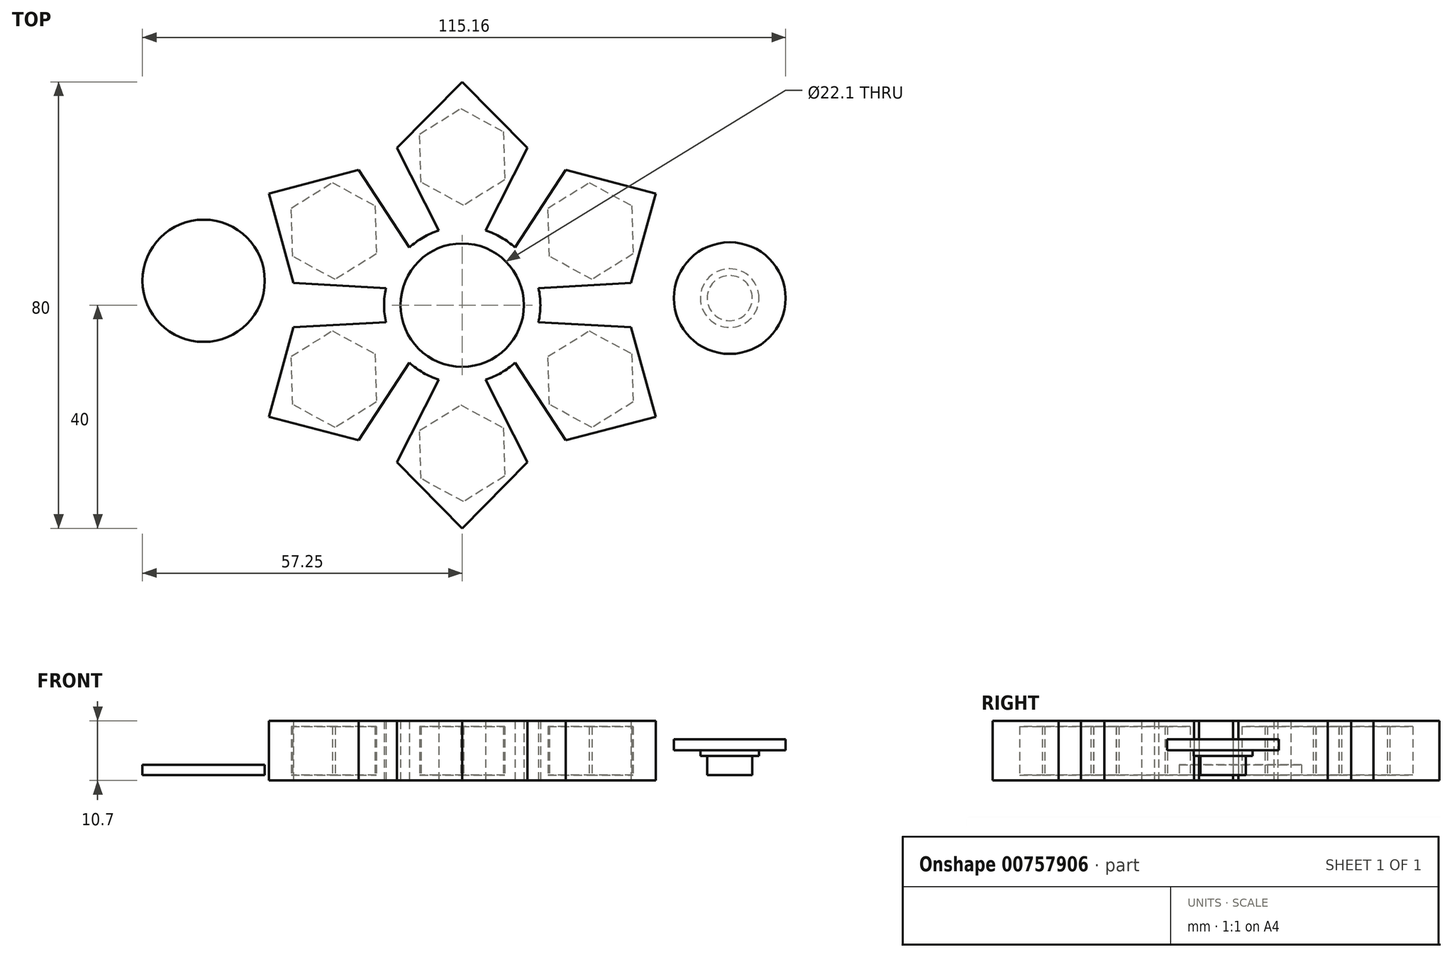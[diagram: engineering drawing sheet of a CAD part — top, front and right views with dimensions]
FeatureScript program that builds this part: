
annotation { "Feature Type Name" : "Feature", "Feature Type Description" : "" }
export const myFeature = defineFeature(function(context is Context, id is Id, definition is map)
    precondition{}
    {
        {
            var Q0;
            Q0=qCreatedBy(makeId("Top.planeOp"),FACE);
            var sketch = newSketch(context, id + "F0", { "sketchPlane" : qUnion([Q0])});
            skCircle(sketch, "E0.cCircle", {"center": v(0, 26.55) * mm, "radius": 8.66 * mm, "construction": true});
            skLineSegment(sketch, "E0.0", {"start": v(7.63, 22.44) * mm, "end": v(0.26, 17.9) * mm});
            skLineSegment(sketch, "E0.1", {"start": v(0.26, 17.9) * mm, "end": v(-7.37, 22) * mm});
            skLineSegment(sketch, "E0.2", {"start": v(-7.37, 22) * mm, "end": v(-7.63, 30.66) * mm});
            skLineSegment(sketch, "E0.3", {"start": v(-7.63, 30.66) * mm, "end": v(-0.26, 35.2) * mm});
            skLineSegment(sketch, "E0.4", {"start": v(-0.26, 35.2) * mm, "end": v(7.37, 31.1) * mm});
            skLineSegment(sketch, "E0.5", {"start": v(7.37, 31.1) * mm, "end": v(7.63, 22.44) * mm});
            skCircle(sketch, "E1", {"center": v(0, 0) * mm, "radius": 40 * mm, "construction": true});
            skCircle(sketch, "E2", {"center": v(0, 0) * mm, "radius": 11.05 * mm});
            skLineSegment(sketch, "E3", {"start": v(0, 40) * mm, "end": v(-11.68, 28.18) * mm});
            skCircle(sketch, "E4", {"center": v(0, 0) * mm, "radius": 14 * mm});
            skLineSegment(sketch, "E5", {"start": v(-11.68, 28.18) * mm, "end": v(-4.19, 13.36) * mm});
            skLineSegment(sketch, "E6", {"start": v(0, 0) * mm, "end": v(0, 60.04) * mm, "construction": true});
            skLineSegment(sketch, "E7.MirrorCS", {"start": v(11.68, 28.18) * mm, "end": v(4.19, 13.36) * mm});
            skLineSegment(sketch, "E8.MirrorCS", {"start": v(0, 40) * mm, "end": v(11.68, 28.18) * mm});
            skLineSegment(sketch, "E9.1.0", {"start": v(-34.64, 20) * mm, "end": v(-30.25, 3.97) * mm});
            skLineSegment(sketch, "E9.1.1", {"start": v(-23.25, 21.93) * mm, "end": v(-15.62, 17.83) * mm});
            skLineSegment(sketch, "E9.1.2", {"start": v(-30.62, 17.38) * mm, "end": v(-23.25, 21.93) * mm});
            skLineSegment(sketch, "E9.1.3", {"start": v(-30.36, 8.72) * mm, "end": v(-30.62, 17.38) * mm});
            skLineSegment(sketch, "E9.1.4", {"start": v(-22.74, 4.62) * mm, "end": v(-30.36, 8.72) * mm});
            skLineSegment(sketch, "E9.1.5", {"start": v(-15.37, 9.17) * mm, "end": v(-22.74, 4.62) * mm});
            skLineSegment(sketch, "E9.1.6", {"start": v(-15.62, 17.83) * mm, "end": v(-15.37, 9.17) * mm});
            skLineSegment(sketch, "E9.1.7", {"start": v(-30.25, 3.97) * mm, "end": v(-13.66, 3.05) * mm});
            skCircle(sketch, "E9.1.8", {"center": v(-23, 13.27) * mm, "radius": 8.66 * mm, "construction": true});
            skLineSegment(sketch, "E9.1.9", {"start": v(-18.57, 24.2) * mm, "end": v(-9.47, 10.3) * mm});
            skLineSegment(sketch, "E9.1.10", {"start": v(-34.64, 20) * mm, "end": v(-18.57, 24.2) * mm});
            skLineSegment(sketch, "E9.2.0", {"start": v(-34.64, -20) * mm, "end": v(-18.57, -24.2) * mm});
            skLineSegment(sketch, "E9.2.1", {"start": v(-30.62, -9.17) * mm, "end": v(-23.25, -4.62) * mm});
            skLineSegment(sketch, "E9.2.2", {"start": v(-30.36, -17.83) * mm, "end": v(-30.62, -9.17) * mm});
            skLineSegment(sketch, "E9.2.3", {"start": v(-22.74, -21.93) * mm, "end": v(-30.36, -17.83) * mm});
            skLineSegment(sketch, "E9.2.4", {"start": v(-15.37, -17.38) * mm, "end": v(-22.74, -21.93) * mm});
            skLineSegment(sketch, "E9.2.5", {"start": v(-15.62, -8.72) * mm, "end": v(-15.37, -17.38) * mm});
            skLineSegment(sketch, "E9.2.6", {"start": v(-23.25, -4.62) * mm, "end": v(-15.62, -8.72) * mm});
            skLineSegment(sketch, "E9.2.7", {"start": v(-18.57, -24.2) * mm, "end": v(-9.47, -10.3) * mm});
            skCircle(sketch, "E9.2.8", {"center": v(-23, -13.27) * mm, "radius": 8.66 * mm, "construction": true});
            skLineSegment(sketch, "E9.2.9", {"start": v(-30.25, -3.97) * mm, "end": v(-13.66, -3.05) * mm});
            skLineSegment(sketch, "E9.2.10", {"start": v(-34.64, -20) * mm, "end": v(-30.25, -3.97) * mm});
            skLineSegment(sketch, "E9.3.0", {"start": v(0, -40) * mm, "end": v(11.68, -28.18) * mm});
            skLineSegment(sketch, "E9.3.1", {"start": v(-7.37, -31.1) * mm, "end": v(-7.63, -22.44) * mm});
            skLineSegment(sketch, "E9.3.2", {"start": v(0.26, -35.2) * mm, "end": v(-7.37, -31.1) * mm});
            skLineSegment(sketch, "E9.3.3", {"start": v(7.63, -30.66) * mm, "end": v(0.26, -35.2) * mm});
            skLineSegment(sketch, "E9.3.4", {"start": v(7.37, -22) * mm, "end": v(7.63, -30.66) * mm});
            skLineSegment(sketch, "E9.3.5", {"start": v(-0.26, -17.9) * mm, "end": v(7.37, -22) * mm});
            skLineSegment(sketch, "E9.3.6", {"start": v(-7.63, -22.44) * mm, "end": v(-0.26, -17.9) * mm});
            skLineSegment(sketch, "E9.3.7", {"start": v(11.68, -28.18) * mm, "end": v(4.19, -13.36) * mm});
            skCircle(sketch, "E9.3.8", {"center": v(0, -26.55) * mm, "radius": 8.66 * mm, "construction": true});
            skLineSegment(sketch, "E9.3.9", {"start": v(-11.68, -28.18) * mm, "end": v(-4.19, -13.36) * mm});
            skLineSegment(sketch, "E9.3.10", {"start": v(0, -40) * mm, "end": v(-11.68, -28.18) * mm});
            skLineSegment(sketch, "E9.4.0", {"start": v(34.64, -20) * mm, "end": v(30.25, -3.97) * mm});
            skLineSegment(sketch, "E9.4.1", {"start": v(23.25, -21.93) * mm, "end": v(15.62, -17.83) * mm});
            skLineSegment(sketch, "E9.4.2", {"start": v(30.62, -17.38) * mm, "end": v(23.25, -21.93) * mm});
            skLineSegment(sketch, "E9.4.3", {"start": v(30.36, -8.72) * mm, "end": v(30.62, -17.38) * mm});
            skLineSegment(sketch, "E9.4.4", {"start": v(22.74, -4.62) * mm, "end": v(30.36, -8.72) * mm});
            skLineSegment(sketch, "E9.4.5", {"start": v(15.37, -9.17) * mm, "end": v(22.74, -4.62) * mm});
            skLineSegment(sketch, "E9.4.6", {"start": v(15.62, -17.83) * mm, "end": v(15.37, -9.17) * mm});
            skLineSegment(sketch, "E9.4.7", {"start": v(30.25, -3.97) * mm, "end": v(13.66, -3.05) * mm});
            skCircle(sketch, "E9.4.8", {"center": v(23, -13.27) * mm, "radius": 8.66 * mm, "construction": true});
            skLineSegment(sketch, "E9.4.9", {"start": v(18.57, -24.2) * mm, "end": v(9.47, -10.3) * mm});
            skLineSegment(sketch, "E9.4.10", {"start": v(34.64, -20) * mm, "end": v(18.57, -24.2) * mm});
            skLineSegment(sketch, "E9.5.0", {"start": v(34.64, 20) * mm, "end": v(18.57, 24.2) * mm});
            skLineSegment(sketch, "E9.5.1", {"start": v(30.62, 9.17) * mm, "end": v(23.25, 4.62) * mm});
            skLineSegment(sketch, "E9.5.2", {"start": v(30.36, 17.83) * mm, "end": v(30.62, 9.17) * mm});
            skLineSegment(sketch, "E9.5.3", {"start": v(22.74, 21.93) * mm, "end": v(30.36, 17.83) * mm});
            skLineSegment(sketch, "E9.5.4", {"start": v(15.37, 17.38) * mm, "end": v(22.74, 21.93) * mm});
            skLineSegment(sketch, "E9.5.5", {"start": v(15.62, 8.72) * mm, "end": v(15.37, 17.38) * mm});
            skLineSegment(sketch, "E9.5.6", {"start": v(23.25, 4.62) * mm, "end": v(15.62, 8.72) * mm});
            skLineSegment(sketch, "E9.5.7", {"start": v(18.57, 24.2) * mm, "end": v(9.47, 10.3) * mm});
            skCircle(sketch, "E9.5.8", {"center": v(23, 13.27) * mm, "radius": 8.66 * mm, "construction": true});
            skLineSegment(sketch, "E9.5.9", {"start": v(30.25, 3.97) * mm, "end": v(13.66, 3.05) * mm});
            skLineSegment(sketch, "E9.5.10", {"start": v(34.64, 20) * mm, "end": v(30.25, 3.97) * mm});
            skSolve(sketch);
        }
        {
            var Q0;
            Q0=makeQuery(id+"F0.imprint","IMPRINT",FACE,{"disambiguationData":[TD([[makeQuery(id+"F0.imprint","IMPRINT",EDGE,{"derivedFrom":sQuery(id+"F0.wireOp",EDGE,"E9.1.0")}),1.0]])]});
            var Q1;
            Q1=makeQuery(id+"F0.imprint","IMPRINT",FACE,{"disambiguationData":[TD([[makeQuery(id+"F0.imprint","IMPRINT",EDGE,{"derivedFrom":sQuery(id+"F0.wireOp",EDGE,"E0.0")}),1.0]])]});
            var Q2;
            Q2=makeQuery(id+"F0.imprint","IMPRINT",FACE,{"disambiguationData":[TD([[makeQuery(id+"F0.imprint","IMPRINT",EDGE,{"derivedFrom":sQuery(id+"F0.wireOp",EDGE,"E9.5.0")}),1.0]])]});
            var Q3;
            Q3=makeQuery(id+"F0.imprint","IMPRINT",FACE,{"disambiguationData":[TD([[makeQuery(id+"F0.imprint","IMPRINT",EDGE,{"derivedFrom":sQuery(id+"F0.wireOp",EDGE,"E9.4.0")}),1.0]])]});
            var Q4;
            Q4=makeQuery(id+"F0.imprint","IMPRINT",FACE,{"disambiguationData":[TD([[makeQuery(id+"F0.imprint","IMPRINT",EDGE,{"derivedFrom":sQuery(id+"F0.wireOp",EDGE,"E9.3.0")}),1.0]])]});
            var Q5;
            Q5=makeQuery(id+"F0.imprint","IMPRINT",FACE,{"disambiguationData":[TD([[makeQuery(id+"F0.imprint","IMPRINT",EDGE,{"derivedFrom":sQuery(id+"F0.wireOp",EDGE,"E9.2.0")}),1.0]])]});
            var Q6;
            Q6=makeQuery(id+"F0.imprint","IMPRINT",FACE,{"disambiguationData":[TD([[makeQuery(id+"F0.imprint","IMPRINT",EDGE,{"derivedFrom":sQuery(id+"F0.wireOp",EDGE,"E2")}),-1.0]])]});
            extrude(context, id + "F1", {"entities" : qUnion([Q0, Q1, Q2, Q3, Q4, Q5, Q6]), "depth" : 8.7 * mm, "offsetDistance" : 25 * mm});
        }
        {
            var Q0;
            Q0=makeQuery(id+"F1.opExtrude","CAP_FACE",FACE,{"disambiguationData":[OSD([sQuery(id+"F0.wireOp",EDGE,"E0.0"),sQuery(id+"F0.wireOp",EDGE,"E0.1"),sQuery(id+"F0.wireOp",EDGE,"E0.2"),sQuery(id+"F0.wireOp",EDGE,"E0.3"),sQuery(id+"F0.wireOp",EDGE,"E0.4"),sQuery(id+"F0.wireOp",EDGE,"E0.5"),sQuery(id+"F0.wireOp",EDGE,"E2"),sQuery(id+"F0.wireOp",EDGE,"E3"),sQuery(id+"F0.wireOp",EDGE,"E4"),sQuery(id+"F0.wireOp",EDGE,"E5"),sQuery(id+"F0.wireOp",EDGE,"E7.MirrorCS"),sQuery(id+"F0.wireOp",EDGE,"E8.MirrorCS"),sQuery(id+"F0.wireOp",EDGE,"E9.1.0"),sQuery(id+"F0.wireOp",EDGE,"E9.1.1"),sQuery(id+"F0.wireOp",EDGE,"E9.1.2"),sQuery(id+"F0.wireOp",EDGE,"E9.1.3"),sQuery(id+"F0.wireOp",EDGE,"E9.1.4"),sQuery(id+"F0.wireOp",EDGE,"E9.1.5"),sQuery(id+"F0.wireOp",EDGE,"E9.1.6"),sQuery(id+"F0.wireOp",EDGE,"E9.1.7"),sQuery(id+"F0.wireOp",EDGE,"E9.1.9"),sQuery(id+"F0.wireOp",EDGE,"E9.1.10"),sQuery(id+"F0.wireOp",EDGE,"E9.2.0"),sQuery(id+"F0.wireOp",EDGE,"E9.2.1"),sQuery(id+"F0.wireOp",EDGE,"E9.2.2"),sQuery(id+"F0.wireOp",EDGE,"E9.2.3"),sQuery(id+"F0.wireOp",EDGE,"E9.2.4"),sQuery(id+"F0.wireOp",EDGE,"E9.2.5"),sQuery(id+"F0.wireOp",EDGE,"E9.2.6"),sQuery(id+"F0.wireOp",EDGE,"E9.2.7"),sQuery(id+"F0.wireOp",EDGE,"E9.2.9"),sQuery(id+"F0.wireOp",EDGE,"E9.2.10"),sQuery(id+"F0.wireOp",EDGE,"E9.3.0"),sQuery(id+"F0.wireOp",EDGE,"E9.3.1"),sQuery(id+"F0.wireOp",EDGE,"E9.3.2"),sQuery(id+"F0.wireOp",EDGE,"E9.3.3"),sQuery(id+"F0.wireOp",EDGE,"E9.3.4"),sQuery(id+"F0.wireOp",EDGE,"E9.3.5"),sQuery(id+"F0.wireOp",EDGE,"E9.3.6"),sQuery(id+"F0.wireOp",EDGE,"E9.3.7"),sQuery(id+"F0.wireOp",EDGE,"E9.3.9"),sQuery(id+"F0.wireOp",EDGE,"E9.3.10"),sQuery(id+"F0.wireOp",EDGE,"E9.4.0"),sQuery(id+"F0.wireOp",EDGE,"E9.4.1"),sQuery(id+"F0.wireOp",EDGE,"E9.4.2"),sQuery(id+"F0.wireOp",EDGE,"E9.4.3"),sQuery(id+"F0.wireOp",EDGE,"E9.4.4"),sQuery(id+"F0.wireOp",EDGE,"E9.4.5"),sQuery(id+"F0.wireOp",EDGE,"E9.4.6"),sQuery(id+"F0.wireOp",EDGE,"E9.4.7"),sQuery(id+"F0.wireOp",EDGE,"E9.4.9"),sQuery(id+"F0.wireOp",EDGE,"E9.4.10"),sQuery(id+"F0.wireOp",EDGE,"E9.5.0"),sQuery(id+"F0.wireOp",EDGE,"E9.5.1"),sQuery(id+"F0.wireOp",EDGE,"E9.5.2"),sQuery(id+"F0.wireOp",EDGE,"E9.5.3"),sQuery(id+"F0.wireOp",EDGE,"E9.5.4"),sQuery(id+"F0.wireOp",EDGE,"E9.5.5"),sQuery(id+"F0.wireOp",EDGE,"E9.5.6"),sQuery(id+"F0.wireOp",EDGE,"E9.5.7"),sQuery(id+"F0.wireOp",EDGE,"E9.5.9"),sQuery(id+"F0.wireOp",EDGE,"E9.5.10")])],"isStart":false});
            var sketch = newSketch(context, id + "F2", { "sketchPlane" : qUnion([Q0])});
            skLineSegment(sketch, "E10.0", {"start": v(-34.64, 20) * mm, "end": v(-30.25, 3.97) * mm});
            skLineSegment(sketch, "E10.1", {"start": v(-34.64, 20) * mm, "end": v(-18.57, 24.2) * mm});
            skLineSegment(sketch, "E10.2", {"start": v(-18.57, 24.2) * mm, "end": v(-9.47, 10.3) * mm});
            skCircle(sketch, "E10.3", {"center": v(0, 0) * mm, "radius": 14 * mm});
            skLineSegment(sketch, "E10.4", {"start": v(-11.68, 28.18) * mm, "end": v(-4.19, 13.36) * mm});
            skLineSegment(sketch, "E10.5", {"start": v(0, 40) * mm, "end": v(-11.68, 28.18) * mm});
            skLineSegment(sketch, "E10.6", {"start": v(0, 40) * mm, "end": v(11.68, 28.18) * mm});
            skLineSegment(sketch, "E10.7", {"start": v(11.68, 28.18) * mm, "end": v(4.19, 13.36) * mm});
            skLineSegment(sketch, "E10.8", {"start": v(18.57, 24.2) * mm, "end": v(9.47, 10.3) * mm});
            skLineSegment(sketch, "E10.9", {"start": v(34.64, 20) * mm, "end": v(18.57, 24.2) * mm});
            skLineSegment(sketch, "E10.10", {"start": v(34.64, 20) * mm, "end": v(30.25, 3.97) * mm});
            skLineSegment(sketch, "E10.11", {"start": v(30.25, 3.97) * mm, "end": v(13.66, 3.05) * mm});
            skLineSegment(sketch, "E10.12", {"start": v(30.25, -3.97) * mm, "end": v(13.66, -3.05) * mm});
            skLineSegment(sketch, "E10.13", {"start": v(34.64, -20) * mm, "end": v(30.25, -3.97) * mm});
            skLineSegment(sketch, "E10.14", {"start": v(34.64, -20) * mm, "end": v(18.57, -24.2) * mm});
            skLineSegment(sketch, "E10.15", {"start": v(18.57, -24.2) * mm, "end": v(9.47, -10.3) * mm});
            skLineSegment(sketch, "E10.16", {"start": v(11.68, -28.18) * mm, "end": v(4.19, -13.36) * mm});
            skLineSegment(sketch, "E10.17", {"start": v(0, -40) * mm, "end": v(11.68, -28.18) * mm});
            skLineSegment(sketch, "E10.18", {"start": v(0, -40) * mm, "end": v(-11.68, -28.18) * mm});
            skLineSegment(sketch, "E10.19", {"start": v(-11.68, -28.18) * mm, "end": v(-4.19, -13.36) * mm});
            skLineSegment(sketch, "E10.20", {"start": v(-18.57, -24.2) * mm, "end": v(-9.47, -10.3) * mm});
            skLineSegment(sketch, "E10.21", {"start": v(-34.64, -20) * mm, "end": v(-18.57, -24.2) * mm});
            skLineSegment(sketch, "E10.22", {"start": v(-34.64, -20) * mm, "end": v(-30.25, -3.97) * mm});
            skLineSegment(sketch, "E10.23", {"start": v(-30.25, -3.97) * mm, "end": v(-13.66, -3.05) * mm});
            skLineSegment(sketch, "E10.24", {"start": v(-30.25, 3.97) * mm, "end": v(-13.66, 3.05) * mm});
            skCircle(sketch, "E10.25", {"center": v(0, 0) * mm, "radius": 11.05 * mm});
            skSolve(sketch);
        }
        {
            var Q0;
            Q0 = qSketchRegion(id + "F2", true);
            extrude(context, id + "F3", {"entities" : qUnion([Q0]), "operationType" : NewBodyOperationType.ADD, "depth" : 1 * mm, "offsetDistance" : 25 * mm});
        }
        {
            var Q0;
            Q0=makeQuery(id+"F1.opExtrude","CAP_FACE",FACE,{"disambiguationData":[OSD([sQuery(id+"F0.wireOp",EDGE,"E0.0"),sQuery(id+"F0.wireOp",EDGE,"E0.1"),sQuery(id+"F0.wireOp",EDGE,"E0.2"),sQuery(id+"F0.wireOp",EDGE,"E0.3"),sQuery(id+"F0.wireOp",EDGE,"E0.4"),sQuery(id+"F0.wireOp",EDGE,"E0.5"),sQuery(id+"F0.wireOp",EDGE,"E2"),sQuery(id+"F0.wireOp",EDGE,"E3"),sQuery(id+"F0.wireOp",EDGE,"E4"),sQuery(id+"F0.wireOp",EDGE,"E5"),sQuery(id+"F0.wireOp",EDGE,"E7.MirrorCS"),sQuery(id+"F0.wireOp",EDGE,"E8.MirrorCS"),sQuery(id+"F0.wireOp",EDGE,"E9.1.0"),sQuery(id+"F0.wireOp",EDGE,"E9.1.1"),sQuery(id+"F0.wireOp",EDGE,"E9.1.2"),sQuery(id+"F0.wireOp",EDGE,"E9.1.3"),sQuery(id+"F0.wireOp",EDGE,"E9.1.4"),sQuery(id+"F0.wireOp",EDGE,"E9.1.5"),sQuery(id+"F0.wireOp",EDGE,"E9.1.6"),sQuery(id+"F0.wireOp",EDGE,"E9.1.7"),sQuery(id+"F0.wireOp",EDGE,"E9.1.9"),sQuery(id+"F0.wireOp",EDGE,"E9.1.10"),sQuery(id+"F0.wireOp",EDGE,"E9.2.0"),sQuery(id+"F0.wireOp",EDGE,"E9.2.1"),sQuery(id+"F0.wireOp",EDGE,"E9.2.2"),sQuery(id+"F0.wireOp",EDGE,"E9.2.3"),sQuery(id+"F0.wireOp",EDGE,"E9.2.4"),sQuery(id+"F0.wireOp",EDGE,"E9.2.5"),sQuery(id+"F0.wireOp",EDGE,"E9.2.6"),sQuery(id+"F0.wireOp",EDGE,"E9.2.7"),sQuery(id+"F0.wireOp",EDGE,"E9.2.9"),sQuery(id+"F0.wireOp",EDGE,"E9.2.10"),sQuery(id+"F0.wireOp",EDGE,"E9.3.0"),sQuery(id+"F0.wireOp",EDGE,"E9.3.1"),sQuery(id+"F0.wireOp",EDGE,"E9.3.2"),sQuery(id+"F0.wireOp",EDGE,"E9.3.3"),sQuery(id+"F0.wireOp",EDGE,"E9.3.4"),sQuery(id+"F0.wireOp",EDGE,"E9.3.5"),sQuery(id+"F0.wireOp",EDGE,"E9.3.6"),sQuery(id+"F0.wireOp",EDGE,"E9.3.7"),sQuery(id+"F0.wireOp",EDGE,"E9.3.9"),sQuery(id+"F0.wireOp",EDGE,"E9.3.10"),sQuery(id+"F0.wireOp",EDGE,"E9.4.0"),sQuery(id+"F0.wireOp",EDGE,"E9.4.1"),sQuery(id+"F0.wireOp",EDGE,"E9.4.2"),sQuery(id+"F0.wireOp",EDGE,"E9.4.3"),sQuery(id+"F0.wireOp",EDGE,"E9.4.4"),sQuery(id+"F0.wireOp",EDGE,"E9.4.5"),sQuery(id+"F0.wireOp",EDGE,"E9.4.6"),sQuery(id+"F0.wireOp",EDGE,"E9.4.7"),sQuery(id+"F0.wireOp",EDGE,"E9.4.9"),sQuery(id+"F0.wireOp",EDGE,"E9.4.10"),sQuery(id+"F0.wireOp",EDGE,"E9.5.0"),sQuery(id+"F0.wireOp",EDGE,"E9.5.1"),sQuery(id+"F0.wireOp",EDGE,"E9.5.2"),sQuery(id+"F0.wireOp",EDGE,"E9.5.3"),sQuery(id+"F0.wireOp",EDGE,"E9.5.4"),sQuery(id+"F0.wireOp",EDGE,"E9.5.5"),sQuery(id+"F0.wireOp",EDGE,"E9.5.6"),sQuery(id+"F0.wireOp",EDGE,"E9.5.7"),sQuery(id+"F0.wireOp",EDGE,"E9.5.9"),sQuery(id+"F0.wireOp",EDGE,"E9.5.10")])],"isStart":true});
            var sketch = newSketch(context, id + "F4", { "sketchPlane" : qUnion([Q0])});
            skCircle(sketch, "E11.0", {"center": v(0, 0) * mm, "radius": 11.05 * mm});
            skCircle(sketch, "E11.1", {"center": v(0, 0) * mm, "radius": 14 * mm});
            skLineSegment(sketch, "E11.2", {"start": v(-11.68, 28.18) * mm, "end": v(-4.19, 13.36) * mm});
            skLineSegment(sketch, "E11.3", {"start": v(11.68, 28.18) * mm, "end": v(4.19, 13.36) * mm});
            skLineSegment(sketch, "E11.4", {"start": v(0, 40) * mm, "end": v(11.68, 28.18) * mm});
            skLineSegment(sketch, "E11.5", {"start": v(0, 40) * mm, "end": v(-11.68, 28.18) * mm});
            skLineSegment(sketch, "E12.1.0", {"start": v(-30.25, 3.97) * mm, "end": v(-13.66, 3.05) * mm});
            skLineSegment(sketch, "E12.1.1", {"start": v(-34.64, 20) * mm, "end": v(-30.25, 3.97) * mm});
            skLineSegment(sketch, "E12.1.2", {"start": v(-34.64, 20) * mm, "end": v(-18.57, 24.2) * mm});
            skLineSegment(sketch, "E12.1.3", {"start": v(-18.57, 24.2) * mm, "end": v(-9.47, 10.3) * mm});
            skLineSegment(sketch, "E12.2.0", {"start": v(-18.57, -24.2) * mm, "end": v(-9.47, -10.3) * mm});
            skLineSegment(sketch, "E12.2.1", {"start": v(-34.64, -20) * mm, "end": v(-18.57, -24.2) * mm});
            skLineSegment(sketch, "E12.2.2", {"start": v(-34.64, -20) * mm, "end": v(-30.25, -3.97) * mm});
            skLineSegment(sketch, "E12.2.3", {"start": v(-30.25, -3.97) * mm, "end": v(-13.66, -3.05) * mm});
            skLineSegment(sketch, "E12.3.0", {"start": v(11.68, -28.18) * mm, "end": v(4.19, -13.36) * mm});
            skLineSegment(sketch, "E12.3.1", {"start": v(0, -40) * mm, "end": v(11.68, -28.18) * mm});
            skLineSegment(sketch, "E12.3.2", {"start": v(0, -40) * mm, "end": v(-11.68, -28.18) * mm});
            skLineSegment(sketch, "E12.3.3", {"start": v(-11.68, -28.18) * mm, "end": v(-4.19, -13.36) * mm});
            skLineSegment(sketch, "E12.4.0", {"start": v(30.25, -3.97) * mm, "end": v(13.66, -3.05) * mm});
            skLineSegment(sketch, "E12.4.1", {"start": v(34.64, -20) * mm, "end": v(30.25, -3.97) * mm});
            skLineSegment(sketch, "E12.4.2", {"start": v(34.64, -20) * mm, "end": v(18.57, -24.2) * mm});
            skLineSegment(sketch, "E12.4.3", {"start": v(18.57, -24.2) * mm, "end": v(9.47, -10.3) * mm});
            skLineSegment(sketch, "E12.5.0", {"start": v(18.57, 24.2) * mm, "end": v(9.47, 10.3) * mm});
            skLineSegment(sketch, "E12.5.1", {"start": v(34.64, 20) * mm, "end": v(18.57, 24.2) * mm});
            skLineSegment(sketch, "E12.5.2", {"start": v(34.64, 20) * mm, "end": v(30.25, 3.97) * mm});
            skLineSegment(sketch, "E12.5.3", {"start": v(30.25, 3.97) * mm, "end": v(13.66, 3.05) * mm});
            skSolve(sketch);
        }
        {
            var Q0;
            Q0=makeQuery(id+"F4.imprint","IMPRINT",FACE,{"disambiguationData":[TD([[makeQuery(id+"F4.imprint","IMPRINT",EDGE,{"derivedFrom":sQuery(id+"F4.wireOp",EDGE,"E11.0")}),1.0]])]});
            var Q1;
            {var subQ2=sQuery(id+"F4.wireOp",EDGE,"E12.1.0");Q1=makeQuery(id+"F4.imprint","IMPRINT",FACE,{"disambiguationData":[TD([[makeQuery(id+"F4.imprint","IMPRINT",EDGE,{"derivedFrom":subQ2}),1.0]])]});}
            var Q2;
            {var subQ2=sQuery(id+"F4.wireOp",EDGE,"E11.2");Q2=makeQuery(id+"F4.imprint","IMPRINT",FACE,{"disambiguationData":[TD([[makeQuery(id+"F4.imprint","IMPRINT",EDGE,{"derivedFrom":subQ2}),1.0]])]});}
            var Q3;
            {var subQ2=sQuery(id+"F4.wireOp",EDGE,"E12.5.0");Q3=makeQuery(id+"F4.imprint","IMPRINT",FACE,{"disambiguationData":[TD([[makeQuery(id+"F4.imprint","IMPRINT",EDGE,{"derivedFrom":subQ2}),1.0]])]});}
            var Q4;
            Q4=makeQuery(id+"F4.imprint","IMPRINT",FACE,{"disambiguationData":[TD([[makeQuery(id+"F4.imprint","IMPRINT",EDGE,{"derivedFrom":makeQuery(id+"F1.opExtrude","CAP_EDGE",EDGE,{"disambiguationData":[OSD([sQuery(id+"F0.wireOp",EDGE,"E9.4.1")])],"isStart":true})}),1.0]])]});
            var Q5;
            Q5=makeQuery(id+"F4.imprint","IMPRINT",FACE,{"disambiguationData":[TD([[makeQuery(id+"F4.imprint","IMPRINT",EDGE,{"derivedFrom":makeQuery(id+"F1.opExtrude","CAP_EDGE",EDGE,{"disambiguationData":[OSD([sQuery(id+"F0.wireOp",EDGE,"E9.3.1")])],"isStart":true})}),1.0]])]});
            var Q6;
            Q6=makeQuery(id+"F4.imprint","IMPRINT",FACE,{"disambiguationData":[TD([[makeQuery(id+"F4.imprint","IMPRINT",EDGE,{"derivedFrom":makeQuery(id+"F1.opExtrude","CAP_EDGE",EDGE,{"disambiguationData":[OSD([sQuery(id+"F0.wireOp",EDGE,"E9.2.1")])],"isStart":true})}),1.0]])]});
            var Q7;
            {var subQ2=sQuery(id+"F4.wireOp",EDGE,"E12.2.0");Q7=makeQuery(id+"F4.imprint","IMPRINT",FACE,{"disambiguationData":[TD([[makeQuery(id+"F4.imprint","IMPRINT",EDGE,{"derivedFrom":subQ2}),1.0]])]});}
            var Q8;
            Q8=makeQuery(id+"F4.imprint","IMPRINT",FACE,{"disambiguationData":[TD([[makeQuery(id+"F4.imprint","IMPRINT",EDGE,{"derivedFrom":makeQuery(id+"F1.opExtrude","CAP_EDGE",EDGE,{"disambiguationData":[OSD([sQuery(id+"F0.wireOp",EDGE,"E9.1.1")])],"isStart":true})}),1.0]])]});
            var Q9;
            {var subQ2=sQuery(id+"F4.wireOp",EDGE,"E12.3.0");Q9=makeQuery(id+"F4.imprint","IMPRINT",FACE,{"disambiguationData":[TD([[makeQuery(id+"F4.imprint","IMPRINT",EDGE,{"derivedFrom":subQ2}),1.0]])]});}
            var Q10;
            Q10=makeQuery(id+"F4.imprint","IMPRINT",FACE,{"disambiguationData":[TD([[makeQuery(id+"F4.imprint","IMPRINT",EDGE,{"derivedFrom":makeQuery(id+"F1.opExtrude","CAP_EDGE",EDGE,{"disambiguationData":[OSD([sQuery(id+"F0.wireOp",EDGE,"E0.0")])],"isStart":true})}),1.0]])]});
            var Q11;
            Q11=makeQuery(id+"F4.imprint","IMPRINT",FACE,{"disambiguationData":[TD([[makeQuery(id+"F4.imprint","IMPRINT",EDGE,{"derivedFrom":makeQuery(id+"F1.opExtrude","CAP_EDGE",EDGE,{"disambiguationData":[OSD([sQuery(id+"F0.wireOp",EDGE,"E9.5.1")])],"isStart":true})}),1.0]])]});
            var Q12;
            {var subQ2=sQuery(id+"F4.wireOp",EDGE,"E12.4.0");Q12=makeQuery(id+"F4.imprint","IMPRINT",FACE,{"disambiguationData":[TD([[makeQuery(id+"F4.imprint","IMPRINT",EDGE,{"derivedFrom":subQ2}),1.0]])]});}
            extrude(context, id + "F5", {"entities" : qUnion([Q0, Q1, Q2, Q3, Q4, Q5, Q6, Q7, Q8, Q9, Q10, Q11, Q12]), "operationType" : NewBodyOperationType.ADD, "depth" : 1 * mm, "offsetDistance" : 25 * mm});
        }
        {
            var Q0;
            Q0=qCreatedBy(makeId("Top.planeOp"),FACE);
            var sketch = newSketch(context, id + "F6", { "sketchPlane" : qUnion([Q0])});
            skCircle(sketch, "E13", {"center": v(-46.3, 4.36) * mm, "radius": 10.95 * mm});
            skSolve(sketch);
        }
        {
            var Q0;
            Q0=makeQuery(id+"F6.imprint","IMPRINT",FACE,{"disambiguationData":[TD([[makeQuery(id+"F6.imprint","IMPRINT",EDGE,{"derivedFrom":sQuery(id+"F6.wireOp",EDGE,"E13")}),1.0]])]});
            extrude(context, id + "F7", {"entities" : qUnion([Q0]), "depth" : 1.8 * mm, "offsetDistance" : 25 * mm});
        }
        {
            var Q0;
            Q0=qCreatedBy(makeId("Top.planeOp"),FACE);
            var sketch = newSketch(context, id + "F8", { "sketchPlane" : qUnion([Q0])});
            skCircle(sketch, "E14", {"center": v(47.9, 1.25) * mm, "radius": 4.04 * mm});
            skSolve(sketch);
        }
        {
            var Q0;
            Q0 = qSketchRegion(id + "F8", true);
            extrude(context, id + "F9", {"entities" : qUnion([Q0]), "depth" : 3.4 * mm, "offsetDistance" : 25 * mm});
        }
        {
            var Q0;
            Q0=makeQuery(id+"F9.opExtrude","CAP_FACE",FACE,{"disambiguationData":[OSD([sQuery(id+"F8.wireOp",EDGE,"E14")])],"isStart":false});
            var sketch = newSketch(context, id + "F10", { "sketchPlane" : qUnion([Q0])});
            skSolve(sketch);
        }
        {
            var Q0;
            Q0=makeQuery(id+"F10.imprint","IMPRINT",FACE,{"disambiguationData":[TD([[makeQuery(id+"F10.imprint","IMPRINT",EDGE,{"derivedFrom":makeQuery(id+"F9.opExtrude","CAP_EDGE",EDGE,{"disambiguationData":[OSD([sQuery(id+"F8.wireOp",EDGE,"E14")])],"isStart":false})}),1.0]])]});
            var sketch = newSketch(context, id + "F11", { "sketchPlane" : qUnion([Q0])});
            skCircle(sketch, "E15.0", {"center": v(47.9, 1.25) * mm, "radius": 4.04 * mm});
            skCircle(sketch, "E16", {"center": v(47.9, 1.25) * mm, "radius": 5.25 * mm});
            skSolve(sketch);
        }
        {
            var Q0;
            Q0=makeQuery(id+"F11.imprint","IMPRINT",FACE,{"disambiguationData":[TD([[makeQuery(id+"F11.imprint","IMPRINT",EDGE,{"derivedFrom":sQuery(id+"F11.wireOp",EDGE,"E15.0")}),-1.0]])]});
            var Q1;
            Q1=makeQuery(id+"F10.imprint","IMPRINT",FACE,{"disambiguationData":[TD([[makeQuery(id+"F10.imprint","IMPRINT",EDGE,{"derivedFrom":makeQuery(id+"F9.opExtrude","CAP_EDGE",EDGE,{"disambiguationData":[OSD([sQuery(id+"F8.wireOp",EDGE,"E14")])],"isStart":false})}),1.0]])]});
            extrude(context, id + "F12", {"entities" : qUnion([Q0, Q1]), "operationType" : NewBodyOperationType.ADD, "depth" : 1 * mm, "offsetDistance" : 25 * mm});
        }
        {
            var Q0;
            Q0=makeQuery(id+"F12.boolean.opBoolean","MERGE",FACE,{"derivedFrom":[makeQuery(id+"F12.opExtrude","CAP_FACE",FACE,{"disambiguationData":[OSD([sQuery(id+"F8.wireOp",EDGE,"E14")])],"isStart":false}),makeQuery(id+"F12.opExtrude","CAP_FACE",FACE,{"disambiguationData":[OSD([sQuery(id+"F11.wireOp",EDGE,"E15.0"),sQuery(id+"F11.wireOp",EDGE,"E16")])],"isStart":false})]});
            var sketch = newSketch(context, id + "F13", { "sketchPlane" : qUnion([Q0])});
            skCircle(sketch, "E17", {"center": v(47.9, 1.25) * mm, "radius": 10 * mm});
            skSolve(sketch);
        }
        {
            var Q0;
            Q0=makeQuery(id+"F13.imprint","IMPRINT",FACE,{"disambiguationData":[TD([[makeQuery(id+"F13.imprint","IMPRINT",EDGE,{"derivedFrom":sQuery(id+"F13.wireOp",EDGE,"E17")}),1.0]])]});
            var Q1;
            Q1=makeQuery(id+"F13.imprint","IMPRINT",FACE,{"disambiguationData":[TD([[makeQuery(id+"F13.imprint","IMPRINT",EDGE,{"derivedFrom":makeQuery(id+"F12.opExtrude","CAP_EDGE",EDGE,{"disambiguationData":[OSD([sQuery(id+"F11.wireOp",EDGE,"E16")])],"isStart":false})}),1.0]])]});
            extrude(context, id + "F14", {"entities" : qUnion([Q0, Q1]), "operationType" : NewBodyOperationType.ADD, "depth" : 2 * mm, "offsetDistance" : 25 * mm});
        }
    });
